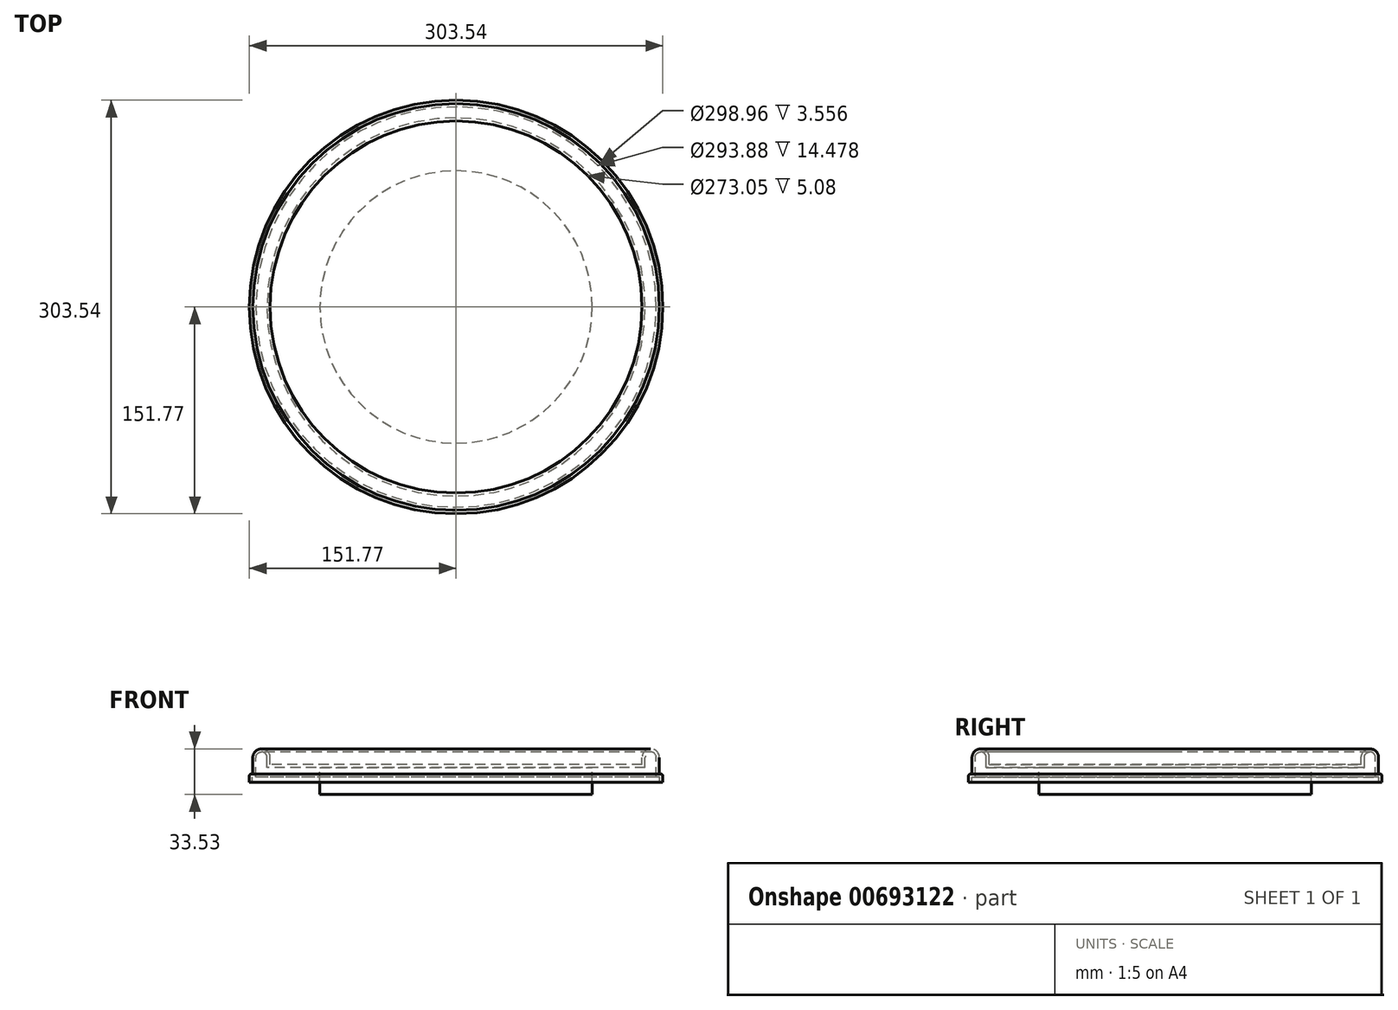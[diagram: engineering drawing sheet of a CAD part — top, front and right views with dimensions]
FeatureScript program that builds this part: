
annotation { "Feature Type Name" : "Feature", "Feature Type Description" : "" }
export const myFeature = defineFeature(function(context is Context, id is Id, definition is map)
    precondition{}
    {
        {
            var Q0;
            Q0=qCreatedBy(makeId("Top.planeOp"),FACE);
            var sketch = newSketch(context, id + "F0", { "sketchPlane" : qUnion([Q0])});
            skCircle(sketch, "E0", {"center": v(0, 0) * mm, "radius": 152.4 * mm});
            skCircle(sketch, "E1", {"center": v(0, 0) * mm, "radius": 136.53 * mm});
            skSolve(sketch);
        }
        {
            var Q0;
            Q0=qCreatedBy(makeId("Front.planeOp"),FACE);
            var sketch = newSketch(context, id + "F1", { "sketchPlane" : qUnion([Q0])});
            skLineSegment(sketch, "E2", {"start": v(-136.53, 0) * mm, "end": v(-136.53, 5.08) * mm});
            skLineSegment(sketch, "E3", {"start": v(-142.88, 11.43) * mm, "end": v(-142.88, 11.43) * mm});
            skLineSegment(sketch, "E4", {"start": v(-149.22, 5.08) * mm, "end": v(-149.22, -7.11) * mm});
            skLineSegment(sketch, "E5", {"start": v(-149.22, -7.11) * mm, "end": v(-150.5, -7.11) * mm});
            skLineSegment(sketch, "E6", {"start": v(-151.77, -8.38) * mm, "end": v(-151.77, -12.95) * mm});
            skLineSegment(sketch, "E7", {"start": v(-151.77, -12.95) * mm, "end": v(-149.48, -12.95) * mm});
            skPoint(sketch, "E8.visualSharp", {"position": v(-149.22, 11.43) * mm});
            skArc(sketch, "E8.filletArc", {"start": v(-142.88, 11.43) * mm, "mid": v(-147.37, 9.57) * mm, "end": v(-149.22, 5.08) * mm});
            skPoint(sketch, "E9.visualSharp", {"position": v(-136.53, 11.43) * mm});
            skArc(sketch, "E9.filletArc", {"start": v(-136.53, 5.08) * mm, "mid": v(-138.38, 9.57) * mm, "end": v(-142.88, 11.43) * mm});
            skPoint(sketch, "E10.visualSharp", {"position": v(-151.77, -7.11) * mm});
            skArc(sketch, "E10.filletArc", {"start": v(-150.5, -7.11) * mm, "mid": v(-151.4, -7.48) * mm, "end": v(-151.76, -8.38) * mm});
            skLineSegment(sketch, "E11.0", {"start": v(-149.48, -9.4) * mm, "end": v(-149.48, -12.95) * mm});
            skLineSegment(sketch, "E11.1", {"start": v(-146.94, -9.4) * mm, "end": v(-149.48, -9.4) * mm});
            skLineSegment(sketch, "E11.2", {"start": v(-138.81, -2.29) * mm, "end": v(-138.81, 5.08) * mm});
            skArc(sketch, "E11.3", {"start": v(-138.81, 5.08) * mm, "mid": v(-140, 7.95) * mm, "end": v(-142.88, 9.14) * mm});
            skArc(sketch, "E11.4", {"start": v(-142.88, 9.14) * mm, "mid": v(-145.75, 7.95) * mm, "end": v(-146.94, 5.08) * mm});
            skLineSegment(sketch, "E11.5", {"start": v(-146.94, 5.08) * mm, "end": v(-146.94, -9.4) * mm});
            skLineSegment(sketch, "E12", {"start": v(-138.81, -2.29) * mm, "end": v(0, -2.29) * mm});
            skLineSegment(sketch, "E13", {"start": v(-136.53, 0) * mm, "end": v(0, 0) * mm});
            skLineSegment(sketch, "E14", {"start": v(0, 0) * mm, "end": v(0, -2.29) * mm});
            skLineSegment(sketch, "E15", {"start": v(0, 44.15) * mm, "end": v(0, -29.05) * mm, "construction": true});
            skSolve(sketch);
        }
        {
            var Q0;
            Q0 = qSketchRegion(id + "F1", true);
            var Q1;
            Q1=sQuery(id+"F1.wireOp",EDGE,"E15");
            revolve(context, id + "F2", {"entities" : qUnion([Q0]), "axis" : qUnion([Q1]), "revolveType" : RevolveType.FULL});
        }
        {
            var Q0;
            Q0=makeQuery(id+"F2.opRevolve","SWEPT_FACE",FACE,{"disambiguationData":[OSD([sQuery(id+"F1.wireOp",EDGE,"E12")])]});
            var sketch = newSketch(context, id + "F3", { "sketchPlane" : qUnion([Q0])});
            skCircle(sketch, "E16", {"center": v(0, 0) * mm, "radius": 100.01 * mm});
            skSolve(sketch);
        }
        {
            var Q0;
            Q0=makeQuery(id+"F3.imprint","IMPRINT",FACE,{"disambiguationData":[TD([[makeQuery(id+"F3.imprint","IMPRINT",EDGE,{"derivedFrom":sQuery(id+"F3.wireOp",EDGE,"E16")}),1.0]])]});
            extrude(context, id + "F4", {"entities" : qUnion([Q0]), "operationType" : NewBodyOperationType.ADD, "depth" : 19.8 * mm, "offsetDistance" : 25.4 * mm});
        }
    });
